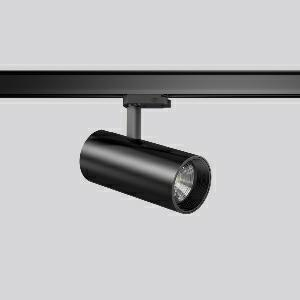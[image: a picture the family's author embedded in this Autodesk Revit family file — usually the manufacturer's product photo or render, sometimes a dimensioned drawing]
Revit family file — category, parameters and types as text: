
# Revit family: deecos_s_mini_742199_003_2_76_97c6
name_source: partatom
category: Lighting Fixtures
units: mm (PartAtom-declared; Revit-internal decimal feet)

## family parameters
Cut with Voids When Loaded = No
Host = Face
Light Source = No
Part Type = Normal
Room Calculation Point = No
Round Connector Dimension = Use Diameter
Shared = No

## types (1)
- DEECOS S mini (1 x LED Modul 927, 2000 lm, 2700)
    Apparent Load = 20 VA
    Approval mark = CE
    CIE Flux Codes = 96 100 100 100 100
    Color Rendering = 92
    Color Temperature = 2700
    Default Elevation = 1800 mm
    Description = Series: DEECOS S mini
LED surface-mounted projector in modern design with no visible cooling ribs. Housing: die-cast aluminium, powder-coated. Rotation range: 356°. Swivel range: 90°. Black plastic ring and recessed LED to prevent glare from the side. Optical assembly with lens made of plastic (polycarbonate) for the best homogeneous light distribution - can be changed without tools. Best colour rendering index Ra>90. With adapter for RZB 3-circuit DALI tracks. Suitable for Track on ceiling, Wall track. High quality converter without flickering and stroboscopic effect. The following accessories can be mounted without use of tools: interchangeable lenses, decorative glasses, honeycomb louvre, clear and frosted diffusers, white interchangeable plastic ring. 
Colour: deep black, matt (RAL 9005)
Diameter: 87 mm
Height: 214 mm
Lamp: LED
Socket: without socket
Colour temperature: 2700K
Colour rendering index (CRI): 92
System power: 20 W
Rated luminous flux: 2000 lm
Luminous efficiency: 100 lm/W
Control gear: Converter, dimmable, DALI
Protection class: I
Type of protection: IP 20
    Height = 214 mm
    Lamp = 1 x LED Modul 927
    Lamp Light Flux = 2000 lm
    Lamp count = 1
    Length = 87 mm
    Lifetime = 50000 h
    Luminous efficacy = 100 lm/W
    Manufacturer = RZB
    ModVariant = No
    Model = 742199.003.2.76
    Mounting Place = Ceiling
    Mounting Type = Rail mounted
    Number of Poles = 1
    OnlyDefault = Yes
    Power Factor = 1
    Product Name = DEECOS S mini
    Product group = Track mounted projectors
    ProductGroupID = 301
    Protection Class = Protection class I
    Protection Degree = IP 20
    RLX_Detail_Level = 1
    RLX_Emergency_Light_Flux = 0 lm
    RLX_Emergency_Type = 0
    RLX_Emergency_Type_DB = No
    RlxData = <blob elided: 39029 chars, md5=fe5dbd36>
    Socket = socket
    Standby Power = 0 W
    System Light Flux = 2000 lm
    System Power = 20 W
    Type Comments = Product without accessories
    Type Image = 741930.003.jpg
    URL = http://relux.com
    VarID = ---
    Voltage = 230 V
    Voltage Range = 220-240 V
    Weight = 0.00 kg
    Width = 0 mm  [stored 0 ft]

note: [stored X ft] marks values corroborated as IEEE doubles in the binary element streams (Revit-internal decimal feet)

## geometry (parser evidence)
native form markers: Blend x4, Sweep x12
no freeform markers — native parametric forms only
